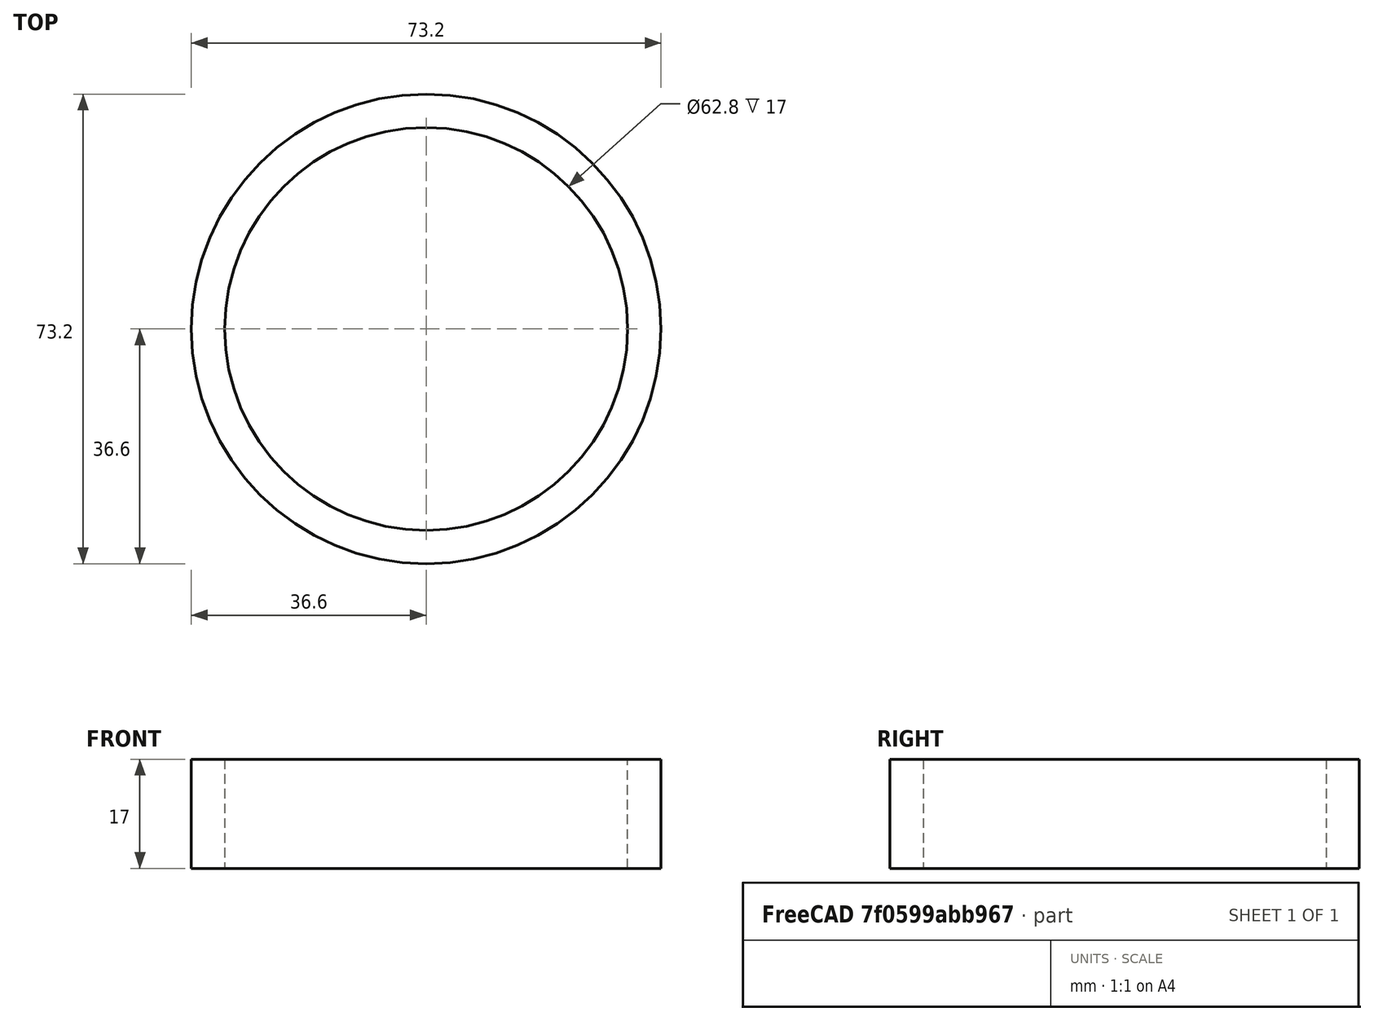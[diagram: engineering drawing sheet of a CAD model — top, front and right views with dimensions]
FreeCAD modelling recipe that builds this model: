
FCSTD DOCUMENT  (FreeCAD 0.18R16093 (Git))
Label: Volante
License: All rights reserved
LicenseURL: http://en.wikipedia.org/wiki/All_rights_reserved
objects: Sketcher::SketchObject×1, PartDesign::Pad×1, PartDesign::Body×1
note: 4 computed .brp shape members not serialized (recipe doc carries the construction recipe); baked Part::Feature solids carry a one-line shape summary decoded from their .brp

FEATURE [Sketcher::SketchObject] Sketch119
  MapMode = 5
  Support = -> [XY_Plane027]
  sketch-geometry (2):
    g0: Circle CenterX=0 CenterY=0 CenterZ=0 NormalX=0 NormalY=0 NormalZ=1 AngleXU=0 Radius=31.4
    g1: Circle CenterX=0 CenterY=0 CenterZ=0 NormalX=0 NormalY=0 NormalZ=1 AngleXU=0 Radius=36.6
  constraints (4):
    c: Radius(g0) = 31.4
    c: Coincident(g1,g-1)
    c: Coincident(g1,g0)
    c: Radius(g1) = 36.6
FEATURE [PartDesign::Pad] Pad064
  Length = 17
  Length2 = 100
  Profile = -> Sketch119
  Type = 0
FEATURE [PartDesign::Body] Body027  label="Volante"
  Group = -> [Sketch119,Pad064]
  Origin = -> Origin027
  Tip = -> Pad064
